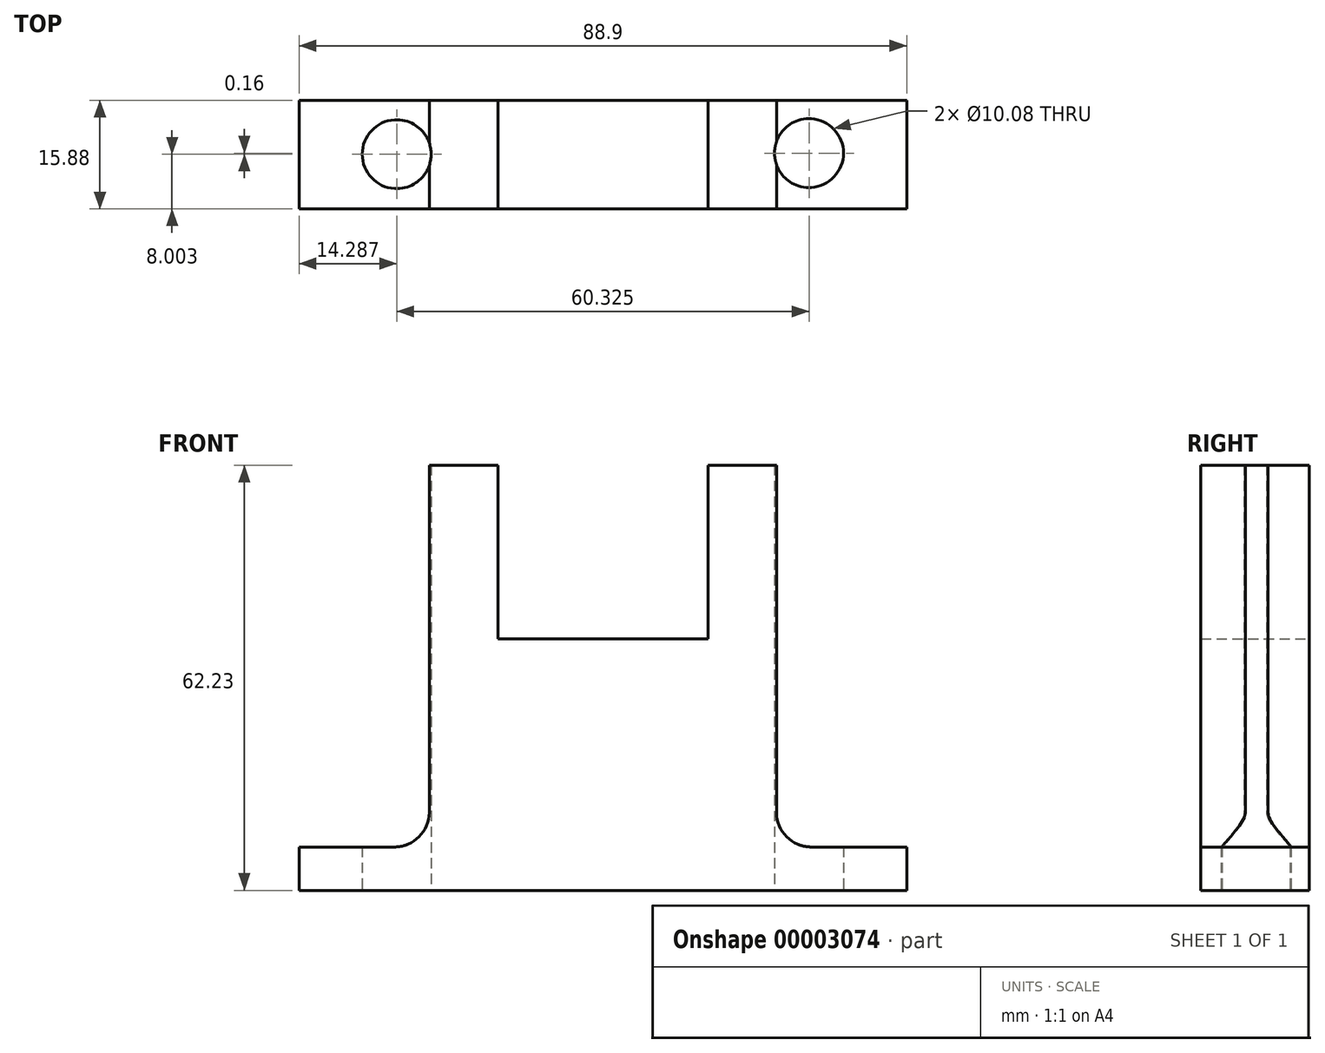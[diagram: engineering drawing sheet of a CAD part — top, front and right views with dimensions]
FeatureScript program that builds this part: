
annotation { "Feature Type Name" : "Feature", "Feature Type Description" : "" }
export const myFeature = defineFeature(function(context is Context, id is Id, definition is map)
    precondition{}
    {
        {
            var Q0;
            Q0=qCreatedBy(makeId("Front.planeOp"),FACE);
            var sketch = newSketch(context, id + "F0", { "sketchPlane" : qUnion([Q0])});
            skLineSegment(sketch, "E0", {"start": v(-44.14, 0) * mm, "end": v(44.76, 0) * mm});
            skLineSegment(sketch, "E1", {"start": v(44.76, 0) * mm, "end": v(44.76, 6.35) * mm});
            skLineSegment(sketch, "E2", {"start": v(44.76, 6.35) * mm, "end": v(25.7, 6.35) * mm});
            skLineSegment(sketch, "E3", {"start": v(25.7, 6.35) * mm, "end": v(25.7, 62.23) * mm});
            skLineSegment(sketch, "E4", {"start": v(25.7, 62.23) * mm, "end": v(15.68, 62.23) * mm});
            skLineSegment(sketch, "E5", {"start": v(15.68, 62.23) * mm, "end": v(15.68, 36.83) * mm});
            skLineSegment(sketch, "E6", {"start": v(15.68, 36.83) * mm, "end": v(-15.06, 36.83) * mm});
            skLineSegment(sketch, "E7", {"start": v(-15.06, 36.83) * mm, "end": v(-15.06, 62.23) * mm});
            skLineSegment(sketch, "E8", {"start": v(-15.06, 62.23) * mm, "end": v(-25.1, 62.23) * mm});
            skLineSegment(sketch, "E9", {"start": v(-25.1, 62.23) * mm, "end": v(-25.1, 6.35) * mm});
            skLineSegment(sketch, "E10", {"start": v(-25.1, 6.35) * mm, "end": v(-44.14, 6.35) * mm});
            skLineSegment(sketch, "E11", {"start": v(-44.14, 6.35) * mm, "end": v(-44.14, 0) * mm});
            skSolve(sketch);
        }
        {
            var Q0;
            Q0=makeQuery(id+"F0.imprint","IMPRINT",FACE,{"disambiguationData":[TD([[makeQuery(id+"F0.imprint","IMPRINT",EDGE,{"derivedFrom":sQuery(id+"F0.wireOp",EDGE,"E0")}),1.0]])]});
            extrude(context, id + "F1", {"entities" : qUnion([Q0]), "depth" : 15.88 * mm});
        }
        {
            var Q0;
            Q0=makeQuery(id+"F1.opExtrude","SWEPT_EDGE",EDGE,{"disambiguationData":[OSD([sQuery(id+"F0.wireOp",EDGE,"E2"),sQuery(id+"F0.wireOp",EDGE,"E3")])]});
            var Q1;
            Q1=makeQuery(id+"F1.opExtrude","SWEPT_EDGE",EDGE,{"disambiguationData":[OSD([sQuery(id+"F0.wireOp",EDGE,"E9"),sQuery(id+"F0.wireOp",EDGE,"E10")])]});
            fillet(context, id + "F2", {"entities" : qUnion([Q0, Q1]), "radius" : 5.08 * mm, "tangentPropagation" : true, "allowEdgeOverflow" : false});
        }
        {
            var Q0;
            Q0=makeQuery(id+"F1.opExtrude","SWEPT_FACE",FACE,{"disambiguationData":[OSD([sQuery(id+"F0.wireOp",EDGE,"E0")])]});
            var sketch = newSketch(context, id + "F3", { "sketchPlane" : qUnion([Q0])});
            skCircle(sketch, "E12", {"center": v(-29.85, 7.88) * mm, "radius": 5.04 * mm});
            skCircle(sketch, "E13", {"center": v(30.47, 7.72) * mm, "radius": 5.04 * mm});
            skLineSegment(sketch, "E14", {"start": v(0.3, 15.88) * mm, "end": v(0.3, 0) * mm, "construction": true});
            skSolve(sketch);
        }
        {
            var Q0;
            Q0=makeQuery(id+"F3.imprint","IMPRINT",FACE,{"disambiguationData":[TD([[makeQuery(id+"F3.imprint","IMPRINT",EDGE,{"derivedFrom":sQuery(id+"F3.wireOp",EDGE,"E12")}),1.0]])]});
            var Q1;
            Q1=makeQuery(id+"F3.imprint","IMPRINT",FACE,{"disambiguationData":[TD([[makeQuery(id+"F3.imprint","IMPRINT",EDGE,{"derivedFrom":sQuery(id+"F3.wireOp",EDGE,"E13")}),1.0]])]});
            extrude(context, id + "F4", {"entities" : qUnion([Q0, Q1]), "operationType" : NewBodyOperationType.REMOVE, "endBound" : BoundingType.THROUGH_ALL, "oppositeDirection" : true, "depth" : 25.4 * mm});
        }
    });
